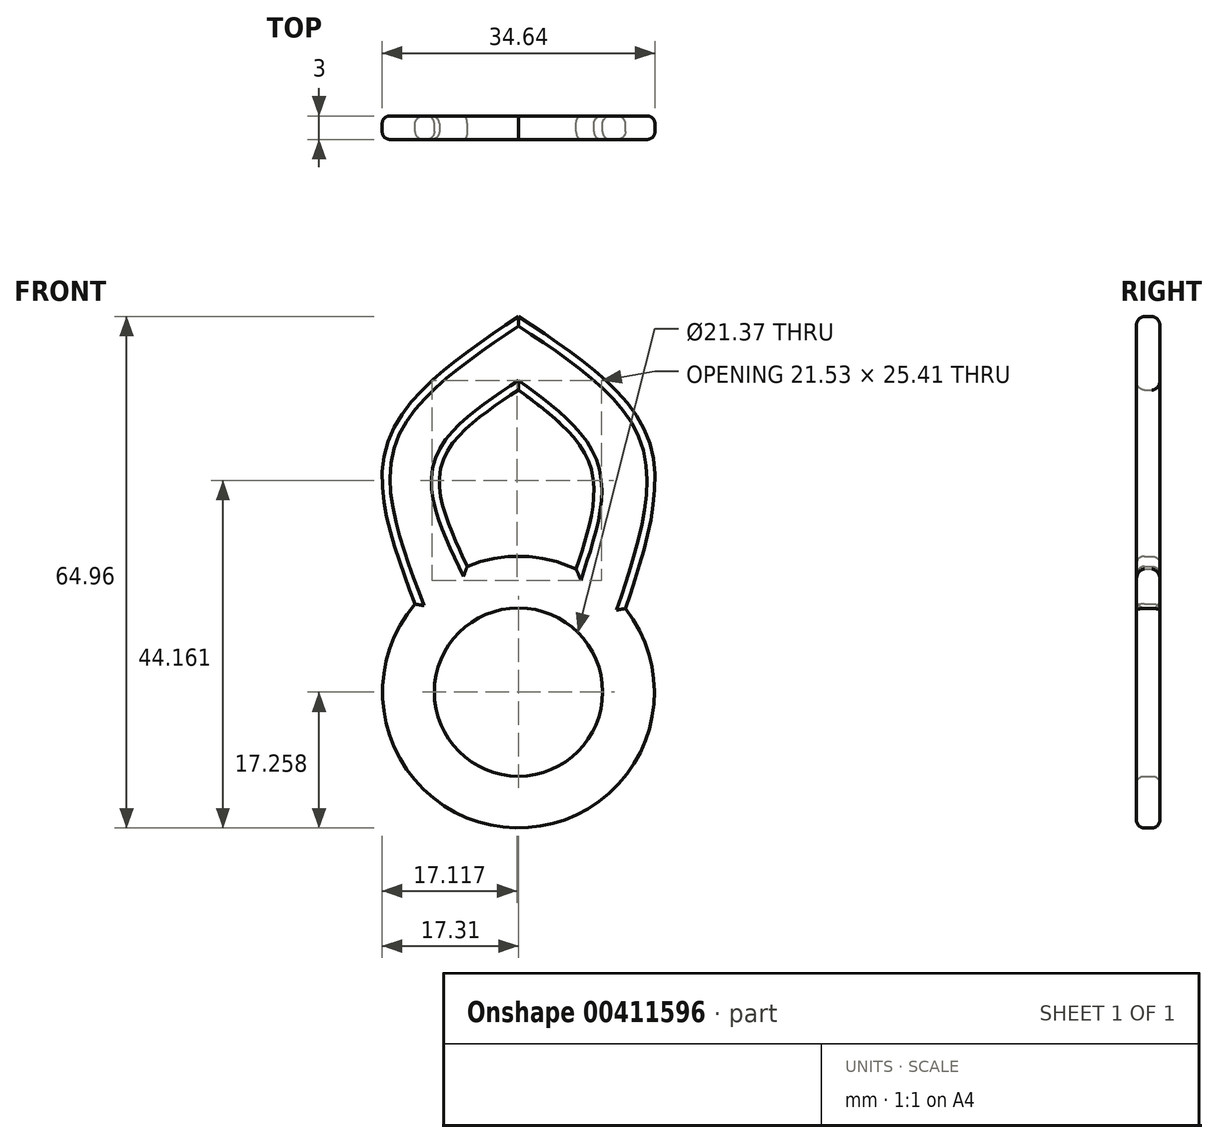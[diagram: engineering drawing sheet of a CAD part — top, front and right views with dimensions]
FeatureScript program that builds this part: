
annotation { "Feature Type Name" : "Feature", "Feature Type Description" : "" }
export const myFeature = defineFeature(function(context is Context, id is Id, definition is map)
    precondition{}
    {
        {
            var Q0;
            Q0=qCreatedBy(makeId("Front.planeOp"),FACE);
            var sketch = newSketch(context, id + "F0", { "sketchPlane" : qUnion([Q0])});
            skLineSegment(sketch, "E0", {"start": v(0, 0) * mm, "end": v(0, -65.77) * mm});
            skLineSegment(sketch, "E1", {"start": v(0, -65.77) * mm, "end": v(25.12, -65.77) * mm});
            skLineSegment(sketch, "E2", {"start": v(0, -65.77) * mm, "end": v(-25.69, -65.77) * mm});
            skCircle(sketch, "E3", {"center": v(0, -47.7) * mm, "radius": 10.68 * mm});
            skCircle(sketch, "E4", {"center": v(0, -47.7) * mm, "radius": 17.25 * mm});
            skFitSpline(sketch, "E5", {"points": [v(0, 0) * mm, v(-16.65, -16.09) * mm, v(-13.13, -36.51) * mm], "startDerivative": vector(-42.6, -28.56) * mm, "endDerivative": vector(16.86, -44.6) * mm});
            skFitSpline(sketch, "E6", {"points": [v(0, -9.31) * mm, v(-9.79, -18.86) * mm, v(-6.5, -31.72) * mm], "startDerivative": vector(-26, -17.2) * mm, "endDerivative": vector(13.1, -27.65) * mm});
            skFitSpline(sketch, "E7", {"points": [v(0, -9.31) * mm, v(9.14, -19.04) * mm, v(7.33, -32.08) * mm], "startDerivative": vector(23.71, -17.67) * mm, "endDerivative": vector(-9.1, -27.87) * mm});
            skFitSpline(sketch, "E8", {"points": [v(0, 0) * mm, v(16.53, -15.68) * mm, v(13.6, -37.08) * mm], "startDerivative": vector(42.35, -27.79) * mm, "endDerivative": vector(-15.32, -46.38) * mm});
            skSolve(sketch);
        }
        {
            var Q0;
            {var subQ2=sQuery(id+"F0.wireOp",EDGE,"E7");Q0=makeQuery(id+"F0.imprint","IMPRINT",FACE,{"disambiguationData":[TD([[makeQuery(id+"F0.imprint","IMPRINT",EDGE,{"derivedFrom":subQ2}),1.0]])]});}
            var Q1;
            {var subQ1=sQuery(id+"F0.wireOp",EDGE,"E0");var subQ4=sQuery(id+"F0.wireOp",EDGE,"E4");var subQ6=makeQuery(id+"F0.imprint","INTERSECT",VERTEX,{"disambiguationData":[OD(1.0)],"derivedFrom":[subQ1,subQ4]});Q1=makeQuery(id+"F0.imprint","IMPRINT",FACE,{"disambiguationData":[TD([[makeQuery(id+"F0.imprint","IMPRINT",EDGE,{"disambiguationData":[TD([[subQ6,-1.0]])],"derivedFrom":subQ1}),-1.0]])]});}
            var Q2;
            {var subQ0=sQuery(id+"F0.wireOp",EDGE,"E5");Q2=makeQuery(id+"F0.imprint","IMPRINT",FACE,{"disambiguationData":[TD([[makeQuery(id+"F0.imprint","IMPRINT",EDGE,{"derivedFrom":subQ0}),1.0]])]});}
            var Q3;
            {var subQ1=sQuery(id+"F0.wireOp",EDGE,"E0");var subQ4=sQuery(id+"F0.wireOp",EDGE,"E4");var subQ8=makeQuery(id+"F0.imprint","INTERSECT",VERTEX,{"disambiguationData":[OD(1.0)],"derivedFrom":[subQ1,subQ4]});Q3=makeQuery(id+"F0.imprint","IMPRINT",FACE,{"disambiguationData":[TD([[makeQuery(id+"F0.imprint","IMPRINT",EDGE,{"disambiguationData":[TD([[subQ8,-1.0]])],"derivedFrom":subQ1}),1.0]])]});}
            extrude(context, id + "F1", {"entities" : qUnion([Q0, Q1, Q2, Q3]), "depth" : 3 * mm});
        }
        {
            var Q0;
            Q0=makeQuery(id+"F1.opExtrude","CAP_FACE",FACE,{"disambiguationData":[OSD([sQuery(id+"F0.wireOp",EDGE,"E3"),sQuery(id+"F0.wireOp",EDGE,"E4"),sQuery(id+"F0.wireOp",EDGE,"E5"),sQuery(id+"F0.wireOp",EDGE,"E6"),sQuery(id+"F0.wireOp",EDGE,"E7"),sQuery(id+"F0.wireOp",EDGE,"E8")])],"isStart":false});
            fillet(context, id + "F2", {"entities" : qUnion([Q0]), "radius" : 1 * mm, "tangentPropagation" : true, "allowEdgeOverflow" : false});
        }
        {
            var Q0;
            Q0=makeQuery(id+"F1.opExtrude","CAP_FACE",FACE,{"disambiguationData":[OSD([sQuery(id+"F0.wireOp",EDGE,"E3"),sQuery(id+"F0.wireOp",EDGE,"E4"),sQuery(id+"F0.wireOp",EDGE,"E5"),sQuery(id+"F0.wireOp",EDGE,"E6"),sQuery(id+"F0.wireOp",EDGE,"E7"),sQuery(id+"F0.wireOp",EDGE,"E8")])],"isStart":true});
            fillet(context, id + "F3", {"entities" : qUnion([Q0]), "radius" : 1 * mm, "tangentPropagation" : true, "allowEdgeOverflow" : false});
        }
    });
